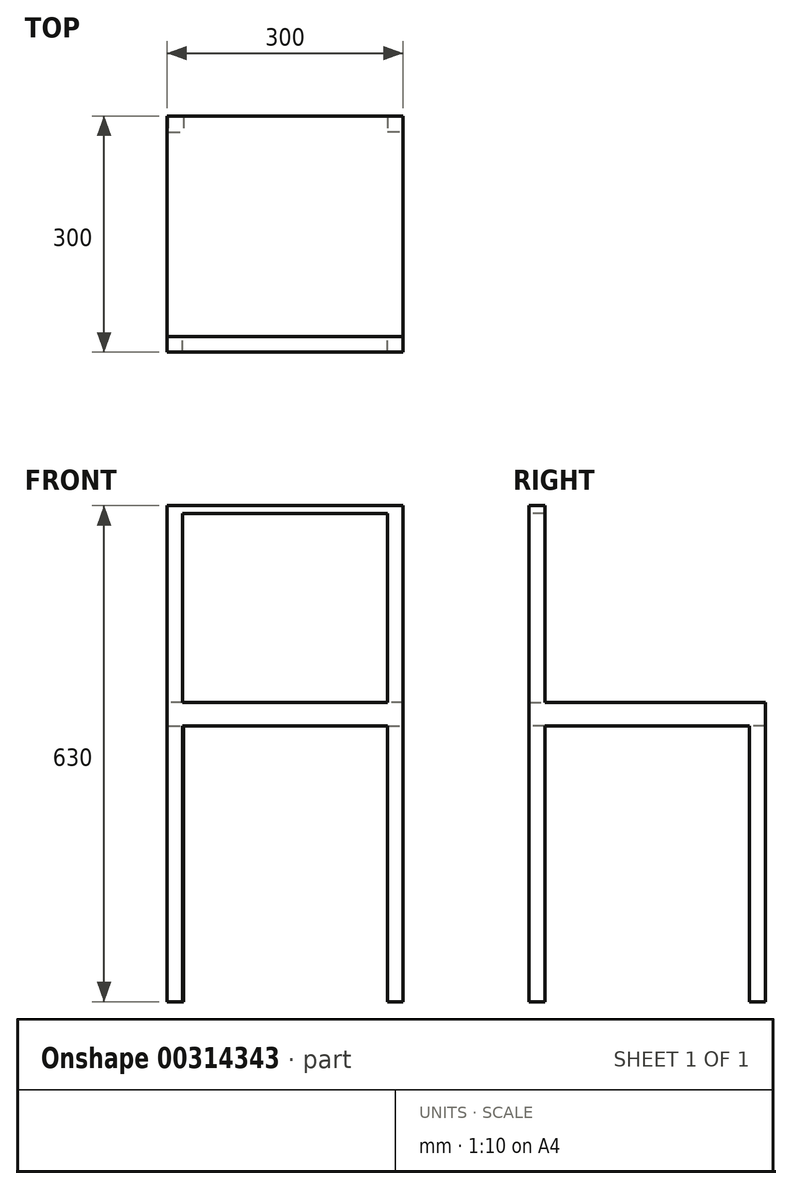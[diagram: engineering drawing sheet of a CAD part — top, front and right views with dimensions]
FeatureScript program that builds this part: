
annotation { "Feature Type Name" : "Feature", "Feature Type Description" : "" }
export const myFeature = defineFeature(function(context is Context, id is Id, definition is map)
    precondition{}
    {
        {
            var Q0;
            Q0=qCreatedBy(makeId("Top.planeOp"),FACE);
            var sketch = newSketch(context, id + "F0", { "sketchPlane" : qUnion([Q0])});
            skLineSegment(sketch, "E0.bottom", {"start": v(-149.75, 153.03) * mm, "end": v(150.25, 153.03) * mm});
            skLineSegment(sketch, "E0.top", {"start": v(-149.75, -146.97) * mm, "end": v(150.25, -146.97) * mm});
            skLineSegment(sketch, "E0.left", {"start": v(-149.75, 153.03) * mm, "end": v(-149.75, -146.97) * mm});
            skLineSegment(sketch, "E0.right", {"start": v(150.25, 153.03) * mm, "end": v(150.25, -146.97) * mm});
            skSolve(sketch);
        }
        {
            var Q0;
            Q0=makeQuery(id+"F0.imprint","IMPRINT",FACE,{"disambiguationData":[TD([[makeQuery(id+"F0.imprint","IMPRINT",EDGE,{"derivedFrom":sQuery(id+"F0.wireOp",EDGE,"E0.bottom")}),-1.0]])]});
            extrude(context, id + "F1", {"entities" : qUnion([Q0]), "depth" : 30 * mm});
        }
        {
            var Q0;
            Q0=makeQuery(id+"F1.opExtrude","CAP_FACE",FACE,{"disambiguationData":[OSD([sQuery(id+"F0.wireOp",EDGE,"E0.bottom"),sQuery(id+"F0.wireOp",EDGE,"E0.top"),sQuery(id+"F0.wireOp",EDGE,"E0.left"),sQuery(id+"F0.wireOp",EDGE,"E0.right")])],"isStart":true});
            var sketch = newSketch(context, id + "F2", { "sketchPlane" : qUnion([Q0])});
            skSolve(sketch);
        }
        {
            var Q0;
            Q0=makeQuery(id+"F2.imprint","IMPRINT",FACE,{"disambiguationData":[TD([[makeQuery(id+"F2.imprint","IMPRINT",EDGE,{"derivedFrom":makeQuery(id+"F1.opExtrude","CAP_EDGE",EDGE,{"disambiguationData":[OSD([sQuery(id+"F0.wireOp",EDGE,"E0.bottom")])],"isStart":true})}),1.0]])]});
            var sketch = newSketch(context, id + "F3", { "sketchPlane" : qUnion([Q0])});
            skLineSegment(sketch, "E1.bottom", {"start": v(-148.48, -152.7) * mm, "end": v(-128.48, -152.7) * mm});
            skLineSegment(sketch, "E1.top", {"start": v(-148.48, -132.7) * mm, "end": v(-128.48, -132.7) * mm});
            skLineSegment(sketch, "E1.left", {"start": v(-148.48, -152.7) * mm, "end": v(-148.48, -132.7) * mm});
            skLineSegment(sketch, "E1.right", {"start": v(-128.48, -152.7) * mm, "end": v(-128.48, -132.7) * mm});
            skLineSegment(sketch, "E2.bottom", {"start": v(-149.75, 126.97) * mm, "end": v(-129.75, 126.97) * mm});
            skLineSegment(sketch, "E2.top", {"start": v(-149.75, 146.97) * mm, "end": v(-129.75, 146.97) * mm});
            skLineSegment(sketch, "E2.left", {"start": v(-149.75, 126.97) * mm, "end": v(-149.75, 146.97) * mm});
            skLineSegment(sketch, "E2.right", {"start": v(-129.75, 126.97) * mm, "end": v(-129.75, 146.97) * mm});
            skLineSegment(sketch, "E3.bottom", {"start": v(130.25, -153.03) * mm, "end": v(150.25, -153.03) * mm});
            skLineSegment(sketch, "E3.top", {"start": v(130.25, -133.03) * mm, "end": v(150.25, -133.03) * mm});
            skLineSegment(sketch, "E3.left", {"start": v(130.25, -153.03) * mm, "end": v(130.25, -133.03) * mm});
            skLineSegment(sketch, "E3.right", {"start": v(150.25, -153.03) * mm, "end": v(150.25, -133.03) * mm});
            skLineSegment(sketch, "E4.bottom", {"start": v(130.25, 126.97) * mm, "end": v(150.25, 126.97) * mm});
            skLineSegment(sketch, "E4.top", {"start": v(130.25, 146.97) * mm, "end": v(150.25, 146.97) * mm});
            skLineSegment(sketch, "E4.left", {"start": v(130.25, 126.97) * mm, "end": v(130.25, 146.97) * mm});
            skLineSegment(sketch, "E4.right", {"start": v(150.25, 126.97) * mm, "end": v(150.25, 146.97) * mm});
            skSolve(sketch);
        }
        {
            var Q0;
            Q0 = qSketchRegion(id + "F3", true);
            extrude(context, id + "F4", {"entities" : qUnion([Q0]), "operationType" : NewBodyOperationType.ADD, "depth" : 350 * mm});
        }
        {
            var Q0;
            Q0=makeQuery(id+"F1.opExtrude","CAP_FACE",FACE,{"disambiguationData":[OSD([sQuery(id+"F0.wireOp",EDGE,"E0.bottom"),sQuery(id+"F0.wireOp",EDGE,"E0.top"),sQuery(id+"F0.wireOp",EDGE,"E0.left"),sQuery(id+"F0.wireOp",EDGE,"E0.right")])],"isStart":false});
            var sketch = newSketch(context, id + "F5", { "sketchPlane" : qUnion([Q0])});
            skLineSegment(sketch, "E5.bottom", {"start": v(150.25, -146.97) * mm, "end": v(130.25, -146.97) * mm});
            skLineSegment(sketch, "E5.top", {"start": v(150.25, -126.97) * mm, "end": v(130.25, -126.97) * mm});
            skLineSegment(sketch, "E5.left", {"start": v(150.25, -146.97) * mm, "end": v(150.25, -126.97) * mm});
            skLineSegment(sketch, "E5.right", {"start": v(130.25, -146.97) * mm, "end": v(130.25, -126.97) * mm});
            skLineSegment(sketch, "E6.bottom", {"start": v(-129.75, -146.97) * mm, "end": v(-149.75, -146.97) * mm});
            skLineSegment(sketch, "E6.top", {"start": v(-129.75, -126.97) * mm, "end": v(-149.75, -126.97) * mm});
            skLineSegment(sketch, "E6.left", {"start": v(-129.75, -146.97) * mm, "end": v(-129.75, -126.97) * mm});
            skLineSegment(sketch, "E6.right", {"start": v(-149.75, -146.97) * mm, "end": v(-149.75, -126.97) * mm});
            skSolve(sketch);
        }
        {
            var Q0;
            Q0 = qSketchRegion(id + "F5", true);
            extrude(context, id + "F6", {"entities" : qUnion([Q0]), "operationType" : NewBodyOperationType.ADD, "depth" : 250 * mm});
        }
        {
            var Q0;
            Q0=makeQuery(id+"F6.opExtrude","SWEPT_FACE",FACE,{"disambiguationData":[OSD([sQuery(id+"F5.wireOp",EDGE,"E5.right")])]});
            var sketch = newSketch(context, id + "F7", { "sketchPlane" : qUnion([Q0])});
            skLineSegment(sketch, "E7.bottom", {"start": v(126.97, 280) * mm, "end": v(146.97, 280) * mm});
            skLineSegment(sketch, "E7.top", {"start": v(126.97, 270) * mm, "end": v(146.97, 270) * mm});
            skLineSegment(sketch, "E7.left", {"start": v(126.97, 280) * mm, "end": v(126.97, 270) * mm});
            skLineSegment(sketch, "E7.right", {"start": v(146.97, 280) * mm, "end": v(146.97, 270) * mm});
            skSolve(sketch);
        }
        {
            var Q0;
            Q0 = qSketchRegion(id + "F7", true);
            extrude(context, id + "F8", {"entities" : qUnion([Q0]), "operationType" : NewBodyOperationType.ADD, "depth" : 260 * mm});
        }
    });
